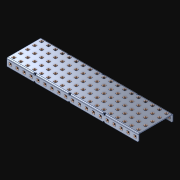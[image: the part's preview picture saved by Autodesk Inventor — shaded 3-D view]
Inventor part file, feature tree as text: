
AUTODESK INVENTOR PART (.ipt)
format: ipt  version: 2021 (Build 250183000, 183)  size: 1,939,456 bytes
history: native  units: in
note: dims shown in document units (in); Inventor stores cm internally (conversion verified against a paired STEP export)
features: extrude x134, other x134, sketch x4, pattern_linear x3
ambient origin geometry x8: Origin, YZ Plane, XZ Plane, XY Plane, X Axis, Y Axis, Z Axis, Center Point
bodies: Solid1 (feature_tree)
feature tree (275):
  pattern_linear  "Rectangular Pattern1"  Spacing1=0.182in  [1 undecoded]
  pattern_linear  "Rectangular Pattern2"  Spacing1=0.046in  [1 undecoded]
  pattern_linear  "Rectangular Pattern3"  Spacing1=0.5in  [1 undecoded]
  extrude  "Extrusion1"  Depth=0.046in
  sketch  "Sketch1"  dims[d0=0.182in]
  other  "Srf1"
  sketch  "Sketch2"  dims[d1=0.046in d2=0.0in]
  other  "Srf2"
  sketch  "Sketch3"  dims[d3=0.182in]
  other  "Srf3"
  other  "Srf4"
  other  "Srf5"
  other  "Srf6"
  other  "Srf7"
  other  "Srf8"
  other  "Srf9"
  other  "Srf10"
  other  "Srf11"
  other  "Srf12"
  other  "Srf13"
  other  "Srf14"
  other  "Srf15"
  other  "Srf16"
  other  "Srf17"
  other  "Srf18"
  other  "Srf19"
  other  "Srf20"
  other  "Srf21"
  other  "Srf38"
  other  "Srf39"
  other  "Srf40"
  other  "Srf41"
  other  "Srf42"
  other  "Srf43"
  other  "Srf44"
  other  "Srf45"
  other  "Srf46"
  other  "Srf47"
  other  "Srf48"
  other  "Srf49"
  other  "Srf50"
  other  "Srf51"
  other  "Srf52"
  other  "Srf53"
  other  "Srf54"
  other  "Srf55"
  other  "Srf72"
  other  "Srf73"
  other  "Srf74"
  other  "Srf75"
  other  "Srf76"
  other  "Srf77"
  other  "Srf78"
  other  "Srf79"
  other  "Srf80"
  other  "Srf81"
  other  "Srf82"
  other  "Srf83"
  other  "Srf84"
  other  "Srf85"
  other  "Srf86"
  other  "Srf87"
  other  "Srf88"
  other  "Srf89"
  other  "Srf90"
  other  "Srf107"
  other  "Srf108"
  other  "Srf109"
  other  "Srf110"
  other  "Srf111"
  other  "Srf112"
  other  "Srf113"
  other  "Srf114"
  other  "Srf115"
  other  "Srf116"
  other  "Srf117"
  other  "Srf118"
  other  "Srf119"
  other  "Srf120"
  other  "Srf121"
  other  "Srf122"
  other  "Srf123"
  other  "Srf124"
  other  "Srf125"
  other  "Srf142"
  other  "Srf143"
  other  "Srf144"
  other  "Srf145"
  other  "Srf146"
  other  "Srf147"
  other  "Srf148"
  other  "Srf149"
  other  "Srf150"
  other  "Srf151"
  other  "Srf152"
  other  "Srf153"
  other  "Srf154"
  other  "Srf155"
  other  "Srf156"
  other  "Srf157"
  other  "Srf158"
  other  "Srf159"
  other  "Srf160"
  other  "Srf177"
  other  "Srf178"
  other  "Srf179"
  other  "Srf180"
  other  "Srf181"
  other  "Srf182"
  other  "Srf183"
  other  "Srf184"
  other  "Srf185"
  other  "Srf186"
  other  "Srf187"
  other  "Srf188"
  other  "Srf189"
  other  "Srf190"
  other  "Srf191"
  other  "Srf192"
  other  "Srf193"
  other  "Srf194"
  other  "Srf195"
  other  "Srf212"
  other  "Srf213"
  other  "Srf214"
  other  "Srf215"
  other  "Srf216"
  other  "Srf217"
  other  "Srf218"
  other  "Srf219"
  other  "Srf220"
  other  "Srf221"
  other  "Srf222"
  other  "Srf223"
  other  "Srf224"
  other  "Srf225"
  other  "Srf226"
  other  "Srf227"
  other  "Srf228"
  other  "Srf229"
  sketch  "Sketch4"  dims[d4=0.046in d5=0.0in d6=0.182in d7=0.046in d8=0.0in d11=0.5in d12=7.4803in d14=0.5in d15=1.9685in d17=0.5in d18=7.4803in d20=0.5in d21=8.0in d22=0.0in]
  parser-record x1  (decoder bookkeeping rows leaked as tree rows — omitted from the tree; the rows remain in map.json)
  extrude  "ExtrusionSrf1"  Depth=0.046in
  extrude  "ExtrusionSrf2"  Depth=0.046in
  extrude  "ExtrusionSrf3"  Depth=0.046in
  extrude  "ExtrusionSrf4"  Depth=0.046in
  extrude  "ExtrusionSrf5"  Depth=0.046in
  extrude  "ExtrusionSrf6"  TaperAngle=0.0deg  [1 undecoded]
  extrude  "ExtrusionSrf7"  [1 undecoded]
  extrude  "ExtrusionSrf8"  [1 undecoded]
  extrude  "ExtrusionSrf9"  [1 undecoded]
  extrude  "ExtrusionSrf10"  [1 undecoded]
  extrude  "ExtrusionSrf11"  [1 undecoded]
  extrude  "ExtrusionSrf12"  [1 undecoded]
  extrude  "ExtrusionSrf13"  [1 undecoded]
  extrude  "ExtrusionSrf14"  [1 undecoded]
  extrude  "ExtrusionSrf15"  [1 undecoded]
  extrude  "ExtrusionSrf16"  [1 undecoded]
  extrude  "ExtrusionSrf17"  [1 undecoded]
  extrude  "ExtrusionSrf18"  [1 undecoded]
  extrude  "ExtrusionSrf19"  [1 undecoded]
  extrude  "ExtrusionSrf20"  [1 undecoded]
  extrude  "ExtrusionSrf21"  [1 undecoded]
  extrude  "ExtrusionSrf38"  [1 undecoded]
  extrude  "ExtrusionSrf39"  [1 undecoded]
  extrude  "ExtrusionSrf40"  [1 undecoded]
  extrude  "ExtrusionSrf41"  [1 undecoded]
  extrude  "ExtrusionSrf42"  [1 undecoded]
  extrude  "ExtrusionSrf43"  [1 undecoded]
  extrude  "ExtrusionSrf44"  [1 undecoded]
  extrude  "ExtrusionSrf45"  [1 undecoded]
  extrude  "ExtrusionSrf46"  [1 undecoded]
  extrude  "ExtrusionSrf47"  [1 undecoded]
  extrude  "ExtrusionSrf48"  [1 undecoded]
  extrude  "ExtrusionSrf49"  [1 undecoded]
  extrude  "ExtrusionSrf50"  [1 undecoded]
  extrude  "ExtrusionSrf51"  [1 undecoded]
  extrude  "ExtrusionSrf52"  [1 undecoded]
  extrude  "ExtrusionSrf53"  [1 undecoded]
  extrude  "ExtrusionSrf54"  [1 undecoded]
  extrude  "ExtrusionSrf55"  [1 undecoded]
  extrude  "ExtrusionSrf72"  [1 undecoded]
  extrude  "ExtrusionSrf73"  [1 undecoded]
  extrude  "ExtrusionSrf74"  [1 undecoded]
  extrude  "ExtrusionSrf75"  [1 undecoded]
  extrude  "ExtrusionSrf76"  [1 undecoded]
  extrude  "ExtrusionSrf77"  [1 undecoded]
  extrude  "ExtrusionSrf78"  [1 undecoded]
  extrude  "ExtrusionSrf79"  [1 undecoded]
  extrude  "ExtrusionSrf80"  [1 undecoded]
  extrude  "ExtrusionSrf81"  [1 undecoded]
  extrude  "ExtrusionSrf82"  [1 undecoded]
  extrude  "ExtrusionSrf83"  [1 undecoded]
  extrude  "ExtrusionSrf84"  [1 undecoded]
  extrude  "ExtrusionSrf85"  [1 undecoded]
  extrude  "ExtrusionSrf86"  [1 undecoded]
  extrude  "ExtrusionSrf87"  [1 undecoded]
  extrude  "ExtrusionSrf88"  [1 undecoded]
  extrude  "ExtrusionSrf89"  [1 undecoded]
  extrude  "ExtrusionSrf90"  [1 undecoded]
  extrude  "ExtrusionSrf107"  [1 undecoded]
  extrude  "ExtrusionSrf108"  [1 undecoded]
  extrude  "ExtrusionSrf109"  [1 undecoded]
  extrude  "ExtrusionSrf110"  [1 undecoded]
  extrude  "ExtrusionSrf111"  [1 undecoded]
  extrude  "ExtrusionSrf112"  [1 undecoded]
  extrude  "ExtrusionSrf113"  [1 undecoded]
  extrude  "ExtrusionSrf114"  [1 undecoded]
  extrude  "ExtrusionSrf115"  [1 undecoded]
  extrude  "ExtrusionSrf116"  [1 undecoded]
  extrude  "ExtrusionSrf117"  [1 undecoded]
  extrude  "ExtrusionSrf118"  [1 undecoded]
  extrude  "ExtrusionSrf119"  [1 undecoded]
  extrude  "ExtrusionSrf120"  [1 undecoded]
  extrude  "ExtrusionSrf121"  [1 undecoded]
  extrude  "ExtrusionSrf122"  [1 undecoded]
  extrude  "ExtrusionSrf123"  [1 undecoded]
  extrude  "ExtrusionSrf124"  [1 undecoded]
  extrude  "ExtrusionSrf125"  [1 undecoded]
  extrude  "ExtrusionSrf142"  [1 undecoded]
  extrude  "ExtrusionSrf143"  [1 undecoded]
  extrude  "ExtrusionSrf144"  [1 undecoded]
  extrude  "ExtrusionSrf145"  [1 undecoded]
  extrude  "ExtrusionSrf146"  [1 undecoded]
  extrude  "ExtrusionSrf147"  [1 undecoded]
  extrude  "ExtrusionSrf148"  [1 undecoded]
  extrude  "ExtrusionSrf149"  [1 undecoded]
  extrude  "ExtrusionSrf150"  [1 undecoded]
  extrude  "ExtrusionSrf151"  [1 undecoded]
  extrude  "ExtrusionSrf152"  [1 undecoded]
  extrude  "ExtrusionSrf153"  [1 undecoded]
  extrude  "ExtrusionSrf154"  [1 undecoded]
  extrude  "ExtrusionSrf155"  [1 undecoded]
  extrude  "ExtrusionSrf156"  [1 undecoded]
  extrude  "ExtrusionSrf157"  [1 undecoded]
  extrude  "ExtrusionSrf158"  [1 undecoded]
  extrude  "ExtrusionSrf159"  [1 undecoded]
  extrude  "ExtrusionSrf160"  [1 undecoded]
  extrude  "ExtrusionSrf177"  [1 undecoded]
  extrude  "ExtrusionSrf178"  [1 undecoded]
  extrude  "ExtrusionSrf179"  [1 undecoded]
  extrude  "ExtrusionSrf180"  [1 undecoded]
  extrude  "ExtrusionSrf181"  [1 undecoded]
  extrude  "ExtrusionSrf182"  [1 undecoded]
  extrude  "ExtrusionSrf183"  [1 undecoded]
  extrude  "ExtrusionSrf184"  [1 undecoded]
  extrude  "ExtrusionSrf185"  [1 undecoded]
  extrude  "ExtrusionSrf186"  [1 undecoded]
  extrude  "ExtrusionSrf187"  [1 undecoded]
  extrude  "ExtrusionSrf188"  [1 undecoded]
  extrude  "ExtrusionSrf189"  [1 undecoded]
  extrude  "ExtrusionSrf190"  [1 undecoded]
  extrude  "ExtrusionSrf191"  [1 undecoded]
  extrude  "ExtrusionSrf192"  [1 undecoded]
  extrude  "ExtrusionSrf193"  [1 undecoded]
  extrude  "ExtrusionSrf194"  [1 undecoded]
  extrude  "ExtrusionSrf195"  [1 undecoded]
  extrude  "ExtrusionSrf212"  [1 undecoded]
  extrude  "ExtrusionSrf213"  [1 undecoded]
  extrude  "ExtrusionSrf214"  [1 undecoded]
  extrude  "ExtrusionSrf215"  [1 undecoded]
  extrude  "ExtrusionSrf216"  [1 undecoded]
  extrude  "ExtrusionSrf217"  [1 undecoded]
  extrude  "ExtrusionSrf218"  [1 undecoded]
  extrude  "ExtrusionSrf219"  [1 undecoded]
  extrude  "ExtrusionSrf220"  [1 undecoded]
  extrude  "ExtrusionSrf221"  [1 undecoded]
  extrude  "ExtrusionSrf222"  [1 undecoded]
  extrude  "ExtrusionSrf223"  [1 undecoded]
  extrude  "ExtrusionSrf224"  [1 undecoded]
  extrude  "ExtrusionSrf225"  [1 undecoded]
  extrude  "ExtrusionSrf226"  [1 undecoded]
  extrude  "ExtrusionSrf227"  [1 undecoded]
  extrude  "ExtrusionSrf228"  [1 undecoded]
  extrude  "ExtrusionSrf229"  [1 undecoded]
note: 131 required parameter values undecoded (feature->parameter linkage not recoverable at this tier; creation-order binding heuristic only, values carry confidence <= 0.55)
